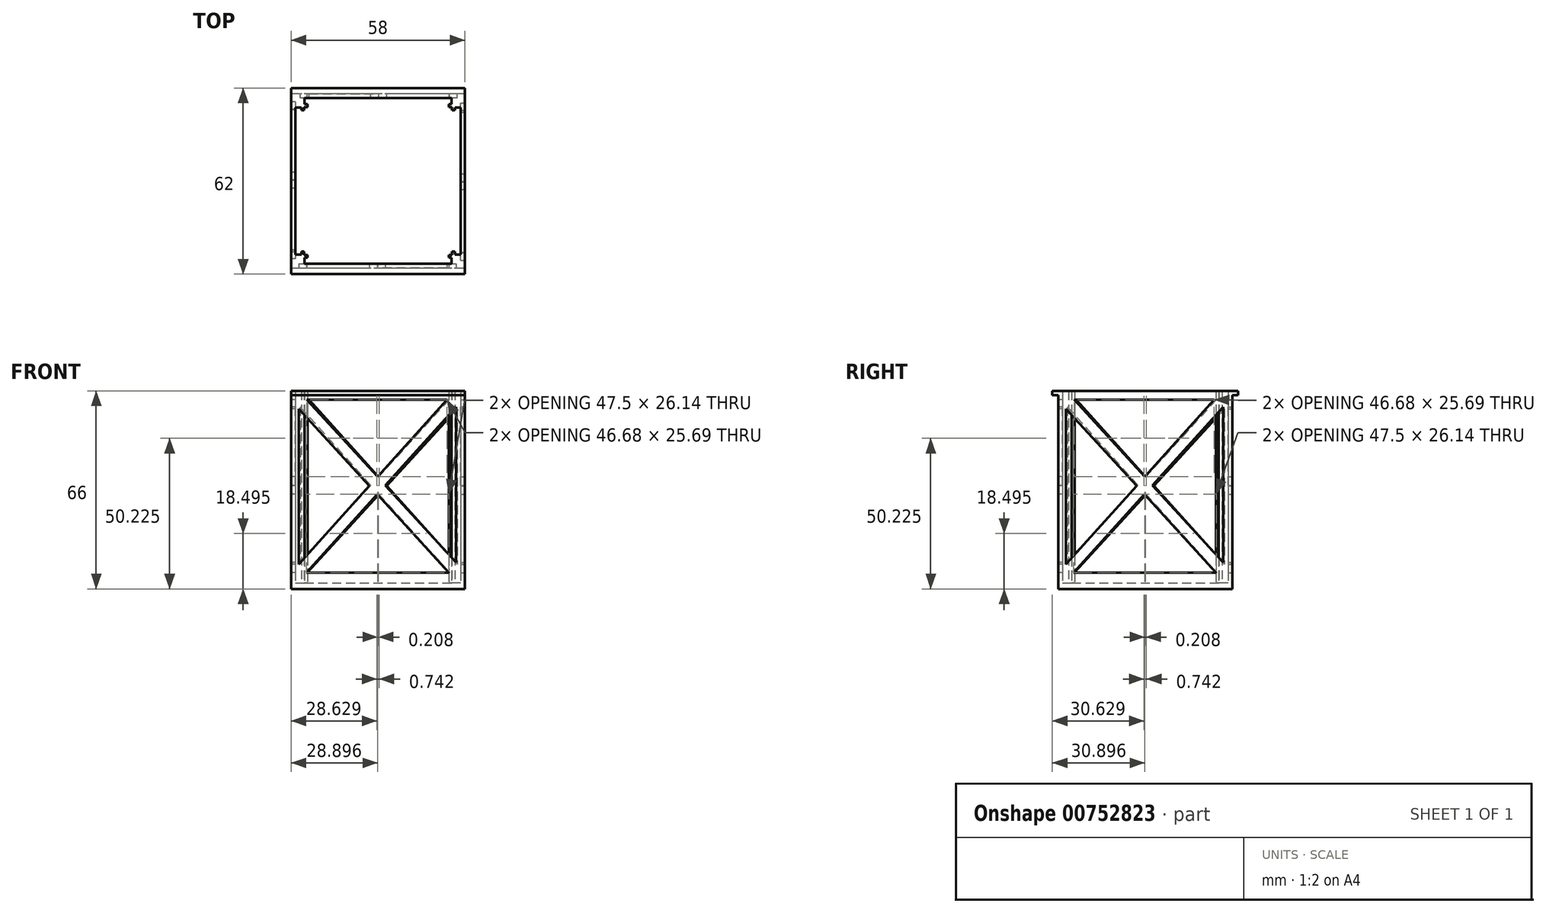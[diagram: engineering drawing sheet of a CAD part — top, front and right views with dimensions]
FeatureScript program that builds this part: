
annotation { "Feature Type Name" : "Feature", "Feature Type Description" : "" }
export const myFeature = defineFeature(function(context is Context, id is Id, definition is map)
    precondition{}
    {
        {
            var Q0;
            Q0=qCreatedBy(makeId("Top.planeOp"),FACE);
            var sketch = newSketch(context, id + "F0", { "sketchPlane" : qUnion([Q0])});
            skLineSegment(sketch, "E0", {"start": v(29, -29) * mm, "end": v(0, 0) * mm, "construction": true});
            skLineSegment(sketch, "E1", {"start": v(29, -29) * mm, "end": v(0, -29) * mm, "construction": true});
            skLineSegment(sketch, "E2", {"start": v(-2.92, -27.6) * mm, "end": v(32.12, -27.6) * mm, "construction": true});
            skLineSegment(sketch, "E3", {"start": v(-4.36, -25.6) * mm, "end": v(31.99, -25.6) * mm, "construction": true});
            skLineSegment(sketch, "E4", {"start": v(24.5, -16.4) * mm, "end": v(24.5, -32.53) * mm, "construction": true});
            skLineSegment(sketch, "E5", {"start": v(0, -29) * mm, "end": v(0, -27.6) * mm});
            skLineSegment(sketch, "E6", {"start": v(0, -27.6) * mm, "end": v(24.5, -27.6) * mm});
            skLineSegment(sketch, "E7", {"start": v(24.5, -27.6) * mm, "end": v(24.5, -25.6) * mm});
            skLineSegment(sketch, "E8", {"start": v(24.5, -25.6) * mm, "end": v(23.55, -25.6) * mm});
            skLineSegment(sketch, "E9", {"start": v(23.55, -25.6) * mm, "end": v(23.55, -24.61) * mm});
            skLineSegment(sketch, "E10", {"start": v(23.55, -24.61) * mm, "end": v(24.61, -24.61) * mm});
            skLineSegment(sketch, "E11", {"start": v(24.61, -24.61) * mm, "end": v(29, -29) * mm});
            skLineSegment(sketch, "E12", {"start": v(0, -29) * mm, "end": v(29, -29) * mm});
            skSolve(sketch);
        }
        {
            var Q0;
            Q0=makeQuery(id+"F0.imprint","IMPRINT",FACE,{"disambiguationData":[TD([[makeQuery(id+"F0.imprint","IMPRINT",EDGE,{"derivedFrom":sQuery(id+"F0.wireOp",EDGE,"E5")}),-1.0]])]});
            extrude(context, id + "F1", {"entities" : qUnion([Q0]), "depth" : 64 * mm, "offsetDistance" : 25 * mm});
        }
        {
            var Q0;
            Q0=makeQuery(id+"F1.opExtrude","SWEPT_BODY",BODY,{"disambiguationData":[OSD([sQuery(id+"F0.wireOp",EDGE,"E5"),sQuery(id+"F0.wireOp",EDGE,"E6"),sQuery(id+"F0.wireOp",EDGE,"E7"),sQuery(id+"F0.wireOp",EDGE,"E8"),sQuery(id+"F0.wireOp",EDGE,"E9"),sQuery(id+"F0.wireOp",EDGE,"E10"),sQuery(id+"F0.wireOp",EDGE,"E11"),sQuery(id+"F0.wireOp",EDGE,"E12")])]});
            var Q1;
            Q1=qCreatedBy(makeId("Right.planeOp"),FACE);
            mirror(context, id + "F2", {"operationType" : NewBodyOperationType.ADD, "entities" : qUnion([Q0]), "mirrorPlane" : qUnion([Q1])});
        }
        {
            var Q0;
            {var subQ0=makeQuery(id+"F1.opExtrude","SWEPT_FACE",FACE,{"disambiguationData":[OSD([sQuery(id+"F0.wireOp",EDGE,"E12")])]});Q0=makeQuery(id+"F2.boolean.opBoolean","MERGE",FACE,{"derivedFrom":[subQ0,makeQuery(id+"F2.opPattern","COPY",FACE,{"derivedFrom":subQ0,"instanceName":"1"})]});}
            var sketch = newSketch(context, id + "F3", { "sketchPlane" : qUnion([Q0])});
            skLineSegment(sketch, "E13.bottom", {"start": v(-26.42, 61.07) * mm, "end": v(25.96, 61.07) * mm});
            skLineSegment(sketch, "E13.top", {"start": v(-26.42, 3.43) * mm, "end": v(25.96, 3.43) * mm});
            skLineSegment(sketch, "E13.left", {"start": v(-26.42, 61.07) * mm, "end": v(-26.42, 3.43) * mm});
            skLineSegment(sketch, "E13.right", {"start": v(25.96, 61.07) * mm, "end": v(25.96, 3.43) * mm});
            skLineSegment(sketch, "E14", {"start": v(-23.71, 61.07) * mm, "end": v(25.96, 6.84) * mm});
            skLineSegment(sketch, "E15", {"start": v(-26.42, 58.08) * mm, "end": v(23.65, 3.43) * mm});
            skLineSegment(sketch, "E16", {"start": v(22.97, 61.07) * mm, "end": v(-26.42, 6.27) * mm});
            skLineSegment(sketch, "E17", {"start": v(-23.86, 3.43) * mm, "end": v(25.96, 58.7) * mm});
            skSolve(sketch);
        }
        {
            var Q0;
            {var subQ0=sQuery(id+"F3.wireOp",EDGE,"E15");var subQ1=sQuery(id+"F3.wireOp",EDGE,"E13.left");var subQ2=makeQuery(id+"F3.imprint","INTERSECT",VERTEX,{"derivedFrom":[subQ1,subQ0]});Q0=makeQuery(id+"F3.imprint","IMPRINT",FACE,{"disambiguationData":[TD([[makeQuery(id+"F3.imprint","IMPRINT",EDGE,{"disambiguationData":[TD([[subQ2,-1.0]])],"derivedFrom":subQ1}),1.0]])]});}
            var Q1;
            {var subQ0=sQuery(id+"F3.wireOp",EDGE,"E14");var subQ1=sQuery(id+"F3.wireOp",EDGE,"E13.bottom");var subQ2=makeQuery(id+"F3.imprint","INTERSECT",VERTEX,{"derivedFrom":[subQ1,subQ0]});Q1=makeQuery(id+"F3.imprint","IMPRINT",FACE,{"disambiguationData":[TD([[makeQuery(id+"F3.imprint","IMPRINT",EDGE,{"disambiguationData":[TD([[subQ2,-1.0]])],"derivedFrom":subQ1}),-1.0]])]});}
            var Q2;
            {var subQ0=sQuery(id+"F3.wireOp",EDGE,"E14");var subQ1=sQuery(id+"F3.wireOp",EDGE,"E13.right");var subQ2=makeQuery(id+"F3.imprint","INTERSECT",VERTEX,{"derivedFrom":[subQ1,subQ0]});Q2=makeQuery(id+"F3.imprint","IMPRINT",FACE,{"disambiguationData":[TD([[makeQuery(id+"F3.imprint","IMPRINT",EDGE,{"disambiguationData":[TD([[subQ2,1.0]])],"derivedFrom":subQ1}),-1.0]])]});}
            var Q3;
            {var subQ0=sQuery(id+"F3.wireOp",EDGE,"E15");var subQ1=sQuery(id+"F3.wireOp",EDGE,"E13.top");var subQ2=makeQuery(id+"F3.imprint","INTERSECT",VERTEX,{"derivedFrom":[subQ1,subQ0]});Q3=makeQuery(id+"F3.imprint","IMPRINT",FACE,{"disambiguationData":[TD([[makeQuery(id+"F3.imprint","IMPRINT",EDGE,{"disambiguationData":[TD([[subQ2,1.0]])],"derivedFrom":subQ1}),1.0]])]});}
            extrude(context, id + "F4", {"entities" : qUnion([Q0, Q1, Q2, Q3]), "operationType" : NewBodyOperationType.REMOVE, "oppositeDirection" : true, "depth" : 1.4 * mm, "offsetDistance" : 25 * mm});
        }
        {
            var Q0;
            {var subQ0=makeQuery(id+"F1.opExtrude","CAP_FACE",FACE,{"disambiguationData":[OSD([sQuery(id+"F0.wireOp",EDGE,"E5"),sQuery(id+"F0.wireOp",EDGE,"E6"),sQuery(id+"F0.wireOp",EDGE,"E7"),sQuery(id+"F0.wireOp",EDGE,"E8"),sQuery(id+"F0.wireOp",EDGE,"E9"),sQuery(id+"F0.wireOp",EDGE,"E10"),sQuery(id+"F0.wireOp",EDGE,"E11"),sQuery(id+"F0.wireOp",EDGE,"E12")])],"isStart":true});Q0=makeQuery(id+"F2.boolean.opBoolean","MERGE",FACE,{"derivedFrom":[subQ0,makeQuery(id+"F2.opPattern","COPY",FACE,{"derivedFrom":subQ0,"instanceName":"1"})]});}
            var sketch = newSketch(context, id + "F5", { "sketchPlane" : qUnion([Q0])});
            skLineSegment(sketch, "E18", {"start": v(-29, 29) * mm, "end": v(0, 0) * mm});
            skLineSegment(sketch, "E19", {"start": v(0, 0) * mm, "end": v(29, 29) * mm});
            skLineSegment(sketch, "E20", {"start": v(29, 29) * mm, "end": v(-29, 29) * mm});
            skSolve(sketch);
        }
        {
            var Q0;
            Q0 = qSketchRegion(id + "F5", true);
            extrude(context, id + "F6", {"entities" : qUnion([Q0]), "operationType" : NewBodyOperationType.ADD, "depth" : 2 * mm, "offsetDistance" : 25 * mm});
        }
        {
            var Q0;
            Q0=qCreatedBy(makeId("Right.planeOp"),FACE);
            var sketch = newSketch(context, id + "F7", { "sketchPlane" : qUnion([Q0])});
            skLineSegment(sketch, "E21", {"start": v(0, 67.54) * mm, "end": v(0, -16.23) * mm, "construction": true});
            skSolve(sketch);
        }
        {
            var Q0;
            Q0=makeQuery(id+"F1.opExtrude","SWEPT_BODY",BODY,{"disambiguationData":[OSD([sQuery(id+"F0.wireOp",EDGE,"E5"),sQuery(id+"F0.wireOp",EDGE,"E6"),sQuery(id+"F0.wireOp",EDGE,"E7"),sQuery(id+"F0.wireOp",EDGE,"E8"),sQuery(id+"F0.wireOp",EDGE,"E9"),sQuery(id+"F0.wireOp",EDGE,"E10"),sQuery(id+"F0.wireOp",EDGE,"E11"),sQuery(id+"F0.wireOp",EDGE,"E12")])]});
            var Q1;
            Q1=sQuery(id+"F7.wireOp",EDGE,"E21");
            circularPattern(context, id + "F8", {"entities" : qUnion([Q0]), "axis" : qUnion([Q1]), "angle" : 360 * degree, "instanceCount" : 4, "equalSpace" : true});
        }
        {
            var Q0;
            {var subQ0=makeQuery(id+"F1.opExtrude","SWEPT_FACE",FACE,{"disambiguationData":[OSD([sQuery(id+"F0.wireOp",EDGE,"E12")])]});Q0=makeQuery(id+"F6.boolean.opBoolean","MERGE",FACE,{"derivedFrom":[makeQuery(id+"F2.boolean.opBoolean","MERGE",FACE,{"derivedFrom":[subQ0,makeQuery(id+"F2.opPattern","COPY",FACE,{"derivedFrom":subQ0,"instanceName":"1"})]}),makeQuery(id+"F6.opExtrude","SWEPT_FACE",FACE,{"disambiguationData":[OSD([sQuery(id+"F5.wireOp",EDGE,"E20")])]})]});}
            var sketch = newSketch(context, id + "F9", { "sketchPlane" : qUnion([Q0])});
            skLineSegment(sketch, "E22.bottom", {"start": v(-29, 64) * mm, "end": v(29, 64) * mm});
            skLineSegment(sketch, "E22.top", {"start": v(-29, 62.56) * mm, "end": v(29, 62.56) * mm});
            skLineSegment(sketch, "E22.left", {"start": v(-29, 64) * mm, "end": v(-29, 62.56) * mm});
            skLineSegment(sketch, "E22.right", {"start": v(29, 64) * mm, "end": v(29, 62.56) * mm});
            skSolve(sketch);
        }
        {
            var Q0;
            Q0 = qSketchRegion(id + "F9", true);
            extrude(context, id + "F10", {"entities" : qUnion([Q0]), "depth" : 2 * mm, "offsetDistance" : 25 * mm});
        }
        {
            var Q0;
            Q0=makeQuery(id+"F10.opExtrude","SWEPT_BODY",BODY,{"disambiguationData":[OSD([sQuery(id+"F9.wireOp",EDGE,"E22.bottom"),sQuery(id+"F9.wireOp",EDGE,"E22.top"),sQuery(id+"F9.wireOp",EDGE,"E22.left"),sQuery(id+"F9.wireOp",EDGE,"E22.right")])]});
            var Q1;
            Q1=qCreatedBy(makeId("Front.planeOp"),FACE);
            mirror(context, id + "F11", {"operationType" : NewBodyOperationType.ADD, "entities" : qUnion([Q0]), "mirrorPlane" : qUnion([Q1])});
        }
    });
